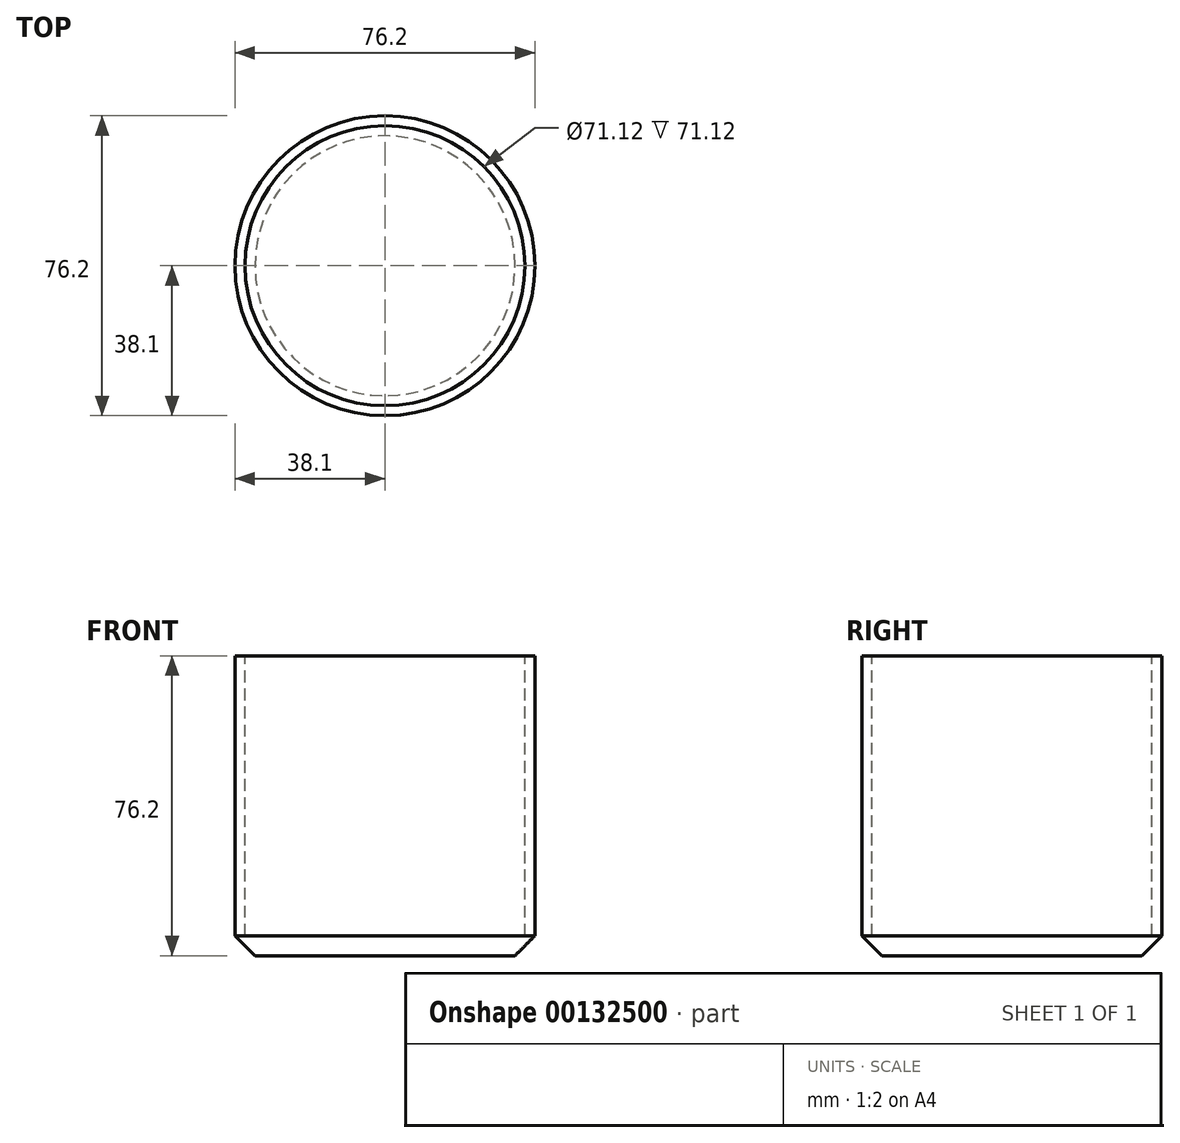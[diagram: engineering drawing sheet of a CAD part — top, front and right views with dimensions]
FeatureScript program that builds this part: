
annotation { "Feature Type Name" : "Feature", "Feature Type Description" : "" }
export const myFeature = defineFeature(function(context is Context, id is Id, definition is map)
    precondition{}
    {
        {
            var Q0;
            Q0=qCreatedBy(makeId("Top.planeOp"),FACE);
            var sketch = newSketch(context, id + "F0", { "sketchPlane" : qUnion([Q0])});
            skCircle(sketch, "E0", {"center": v(0, 0) * mm, "radius": 38.1 * mm});
            skSolve(sketch);
        }
        {
            var Q0;
            Q0=makeQuery(id+"F0.imprint","IMPRINT",FACE,{"disambiguationData":[TD([[makeQuery(id+"F0.imprint","IMPRINT",EDGE,{"derivedFrom":sQuery(id+"F0.wireOp",EDGE,"E0")}),1.0]])]});
            extrude(context, id + "F1", {"entities" : qUnion([Q0]), "depth" : 76.2 * mm});
        }
        {
            var Q0;
            Q0=makeQuery(id+"F1.opExtrude","CAP_FACE",FACE,{"disambiguationData":[OSD([sQuery(id+"F0.wireOp",EDGE,"E0")])],"isStart":false});
            var sketch = newSketch(context, id + "F2", { "sketchPlane" : qUnion([Q0])});
            skCircle(sketch, "E1", {"center": v(0, 0) * mm, "radius": 35.56 * mm});
            skSolve(sketch);
        }
        {
            var Q0;
            Q0=makeQuery(id+"F2.imprint","IMPRINT",FACE,{"disambiguationData":[TD([[makeQuery(id+"F2.imprint","IMPRINT",EDGE,{"derivedFrom":sQuery(id+"F2.wireOp",EDGE,"E1")}),1.0]])]});
            extrude(context, id + "F3", {"entities" : qUnion([Q0]), "operationType" : NewBodyOperationType.REMOVE, "oppositeDirection" : true, "depth" : 71.12 * mm});
        }
        {
            var Q0;
            Q0=makeQuery(id+"F1.opExtrude","CAP_EDGE",EDGE,{"disambiguationData":[OSD([sQuery(id+"F0.wireOp",EDGE,"E0")])],"isStart":true});
            chamfer(context, id + "F4", {"entities" : qUnion([Q0]), "width" : 5.08 * mm, "tangentPropagation" : true});
        }
    });
